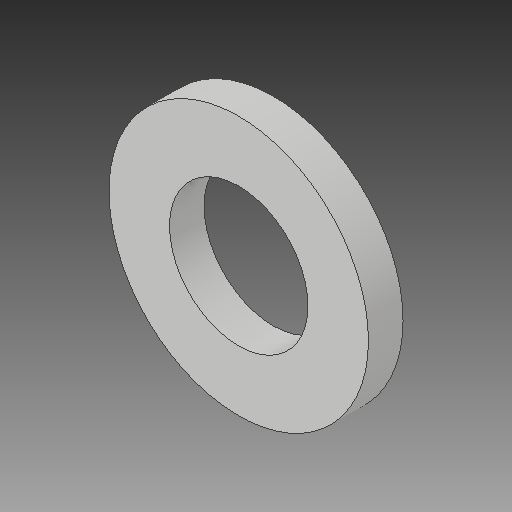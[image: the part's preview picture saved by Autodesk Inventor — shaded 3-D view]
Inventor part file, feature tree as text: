
AUTODESK INVENTOR PART (.ipt)
format: ipt  version: 2018 (Build 220112000, 112)  size: 93,696 bytes
history: native  units: mm
features: other x3, extrude x1, sketch x1, reference x1
ambient origin geometry x8: Origin, YZ Plane, XZ Plane, XY Plane, X Axis, Y Axis, Z Axis, Center Point
bodies: Solid1 (feature_tree)
feature tree (6):
  extrude  "Extrusion1"  Depth=0.8mm
  sketch  "Sketch1"  dims[d0=3.2mm d1=6.0mm d2=0.8mm d3=0.0mm]
  reference  "Reference1"
  other  "<userpath>\OneDrive\SL-Inventor\SL-Beast 3D Printer\x-aXIS-aSSEMBLY.iam"
  other  "x-aXIS-aSSEMBLY.iam"
  other  "M1173041- NEMA 17:1"
